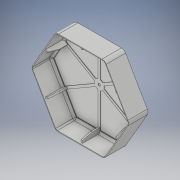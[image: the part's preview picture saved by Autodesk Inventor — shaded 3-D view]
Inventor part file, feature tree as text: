
AUTODESK INVENTOR PART (.ipt)
format: ipt  version: 2019 (Build 230136000, 136)  size: 304,640 bytes
history: native  units: mm
features: sketch x7, extrude x4, plane x3, fillet x3, other x3, projected_geometry x3, shell x1, pattern_circular x1
ambient origin geometry x8: Origin, YZ Plane, XZ Plane, XY Plane, X Axis, Y Axis, Z Axis, Center Point
bodies: Solid1 (feature_tree)
feature tree (25):
  extrude  "Extrusion1"  Depth=40.0mm TaperAngle=0.0deg
  shell  "Shell1"  Thickness=1.5mm
  plane  "Work Plane1"
  plane  "Work Plane2"
  plane  "Work Plane3"
  extrude  "Extrusion5"  Depth=10.0mm
  extrude  "Extrusion6"  Depth=5.0mm
  extrude  "Extrusion8"  TaperAngle=60.0deg  [1 undecoded]
  pattern_circular  "Circular Pattern1"  [2 undecoded]
  fillet  "Fillet1"  Radius=5.0mm
  fillet  "Fillet2"  Radius=2.0mm
  fillet  "Fillet4"  Radius=3.0mm
  sketch  "Sketch5"  dims[d12=1.0mm d37=5.0mm]
  sketch  "Sketch6"  dims[d44=10.0mm d45=60.0deg]
  sketch  "Sketch7"  dims[d46=90.0deg]
  other  "Work Axis4"
  other  "Work Axis5"
  other  "Work Axis6"
  sketch  "Sketch1"  dims[d0=175.0mm d2=40.0mm d3=0.0mm d4=1.5mm]
  sketch  "Sketch4"  dims[d10=4.0mm d11=10.0mm]
  projected_geometry  "Projected Loop3"
  sketch  "Sketch8"  dims[d47=90.0deg]
  projected_geometry  "Projected Loop4"
  sketch  "Sketch9"  dims[d52=5.5mm d53=0.75mm d54=0.0mm d55=5.0mm d56=2.0mm d57=3.0mm d58=10.0mm d59=36.0mm d60=0.0mm d70=60.0mm d72=360.0deg d74=60.0mm d75=360.0deg d77=5.0mm d78=20.0mm d79=20.0mm d80=0.0mm]
  projected_geometry  "Projected Loop5"
note: 3 required parameter values undecoded (feature->parameter linkage not recoverable at this tier; creation-order binding heuristic only, values carry confidence <= 0.55)
